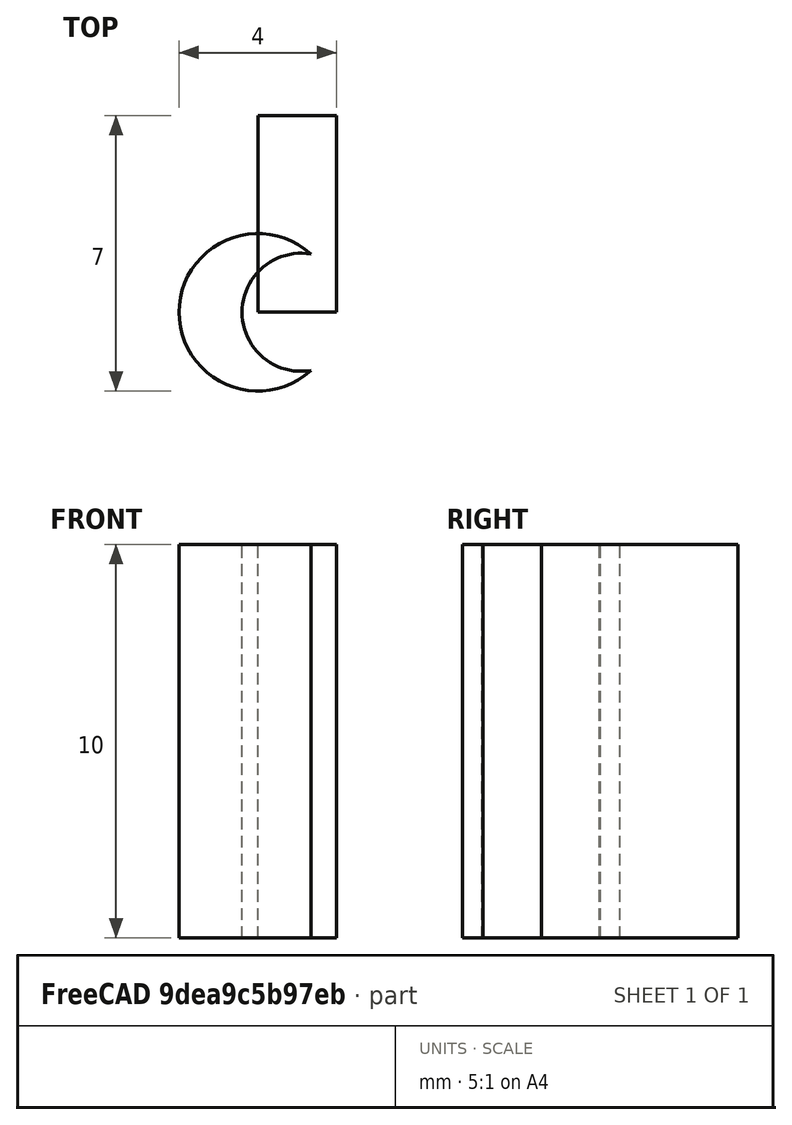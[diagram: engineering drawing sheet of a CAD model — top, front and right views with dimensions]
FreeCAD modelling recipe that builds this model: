
FCSTD DOCUMENT  (FreeCAD 0.17R11508 (Git))
Label: cylinderAFo
License: All rights reserved
LicenseURL: http://en.wikipedia.org/wiki/All_rights_reserved
objects: Fem::FemSolverObjectPython×2, App::MaterialObjectPython×2, Fem::ConstraintDisplacement×2, Fem::ConstraintFixed×2, Fem::FemMeshObjectPython×2, Fem::FemResultObjectPython×2, Fem::FemAnalysisPython×2, Part::Feature×1, Part::Box×1
note: 2 computed .brp shape members not serialized (recipe doc carries the construction recipe); baked Part::Feature solids carry a one-line shape summary decoded from their .brp

FEATURE [Fem::FemSolverObjectPython] CalculiX  # FEM object (typed FeaturePython)
  AnalysisType = 0
  EigenmodeHighLimit = 1000000
  EigenmodeLowLimit = 0
  EigenmodesCount = 10
  GeometricalNonlinearity = 0
  IterationsControlParameterCutb = 0.25,0.5,0.75,0.85,,,1.5,
  IterationsControlParameterIter = 4,8,9,200,10,400,,200,,
  IterationsControlParameterTimeUse = false
  IterationsThermoMechMaximum = 2000
  IterationsUserDefinedIncrementations = false
  IterationsUserDefinedTimeStepLength = false
  MaterialNonlinearity = 0
  MatrixSolverType = 0
  SolverType = FemSolverCalculix
  SplitInputWriter = false
  ThermoMechSteadyState = true
  TimeEnd = 1
  TimeInitialStep = 0.01
FEATURE [App::MaterialObjectPython] SolidMaterial  # material (typed FeaturePython)
  Category = 0
  Material = Density=1300.0 kg/m^3,+11 more (map truncated)
FEATURE [Part::Feature] Cut001
  shape: bbox 3.345 x 4 x 10 mm, 4 faces (baked)
FEATURE [Fem::ConstraintDisplacement] FemConstraintDisplacement
  NormalDirection = (0,0,1)
  Normals = (1) [(0,0,1)]
  Points = (1) [(-2,0,10)]
  References = -> [Cut001]
  rotxFix = false
  rotxFree = false
  rotyFix = false
  rotyFree = true
  rotzFix = true
  rotzFree = false
  xDisplacement = -0.0541705
  xFix = false
  xFree = false
  xRotation = 10
  yDisplacement = 0.0230125
  yFix = false
  yFree = false
  yRotation = 0
  zDisplacement = 0.00226832
  zFix = false
  zFree = false
  zRotation = 50
FEATURE [Fem::ConstraintFixed] FemConstraintFixed
  NormalDirection = (0,0,-1)
  Normals = (1) [(0,0,-1)]
  Points = (1) [(-2,0,0)]
  References = -> [Cut001]
FEATURE [Fem::FemMeshObjectPython] FEMMeshGMSH  # FEM object (typed FeaturePython)
  Algorithm2D = 0
  Algorithm3D = 0
  CharacteristicLengthMax = 0
  CharacteristicLengthMin = 0
  CoherenceMesh = true
  ElementDimension = 0
  ElementOrder = 1
  GeometryTolerance = 1e-06
  HighOrderOptimize = false
  OptimizeNetgen = false
  OptimizeStd = true
  Part = -> Cut001
  RecombineAll = false
FEATURE [Fem::FemResultObjectPython] CalculiX_static_results  # FEM object (typed FeaturePython)
  DisplacementLengths = [0.0588996,0.0588996,0,0,0.0588996,0.0588996,0.0588996,0.0588996,0.0588996,0.0588996,0.0588996,0.013727,0.0273456,0.0407869,0.0515742,0.00728433,0.0203832,0.0341927,0.0467081,0.0551273,0,0,0,0,0,0,0,0.0101896,0.0242184,0.0402139,0.0533005,+271 more]
  DisplacementVectors = (302) [(-0.0541705,0.0230125,0.00226832),(-0.0541705,0.0230125,0.00226832),(0,0,0),(0,0,0),(-0.0541705,0.0230125,0.00226832),+297 more]
  Eigenmode = 0
  EigenmodeFrequency = 0
  MaxShear = [5.5501,9.78783,10.6198,6.36073,3.63674,5.02008,1.77972,0.767103,5.05763,2.59359,5.59522,7.77964,3.28659,2.6727,7.10986,9.93378,5.64332,0.767785,4.88157,9.01165,2.95717,4.62495,2.19645,1.20809,4.42554,2.1266,5.85524,5.90892,2.41082,1.59936,+272 more]
  Mesh = -> FEMMeshGMSH
  NodeNumbers = [1,2,3,4,5,6,7,8,9,10,11,12,13,14,15,16,17,18,19,20,21,22,23,24,25,26,27,28,29,30,31,32,33,34,35,36,37,38,39,40,41,42,43,44,45,46,47,48,49,50,51,52,53,54,55,56,57,58,59,60,61,62,63,64,65,66,67,68,69,+233 more]
  PrincipalMax = [-3.16561,-4.33294,25.5958,16.2608,11.3628,17.2628,-0.330382,-0.302449,20.1892,9.8337,-3.99133,15.0806,6.56805,0.291143,0.37496,18.3907,11.0801,1.54534,0.552377,0.824055,-3.63394,-6.69301,5.5292,3.45117,-8.94039,-3.3151,17.4186,11.6049,+274 more]
  PrincipalMed = [-5.2038,-9.5514,9.6445,6.25228,4.92049,7.73802,-1.41141,-0.916493,10.8538,5.33106,-6.73552,0.682284,0.0931949,0.0262324,-0.0293278,0.690424,0.0876384,0.32165,0.167359,-1.33784,-4.2703,-7.25013,2.14533,1.86964,-9.63158,-4.03354,8.35848,+275 more]
  PrincipalMin = [-14.2658,-23.9086,4.35625,3.53934,4.08931,7.22268,-3.88982,-1.83666,10.0739,4.64653,-15.1818,-0.478681,-0.00512452,-5.05426,-13.8448,-1.47687,-0.206507,0.00976902,-9.21075,-17.1993,-9.54829,-15.9429,1.13631,1.035,-17.7915,-7.56831,5.70807,+275 more]
  ResultType = FemResultMechanical
  Stats = [-0.0541705,-0.0273203,0,-0.000334248,0.0115734,0.023171,-0.00876269,0.00251576,0.0171067,0,0.0302706,0.0588996,0.879918,5.38831,19.1511,-8.94039,3.31382,25.5958,-9.63158,0.0830932,10.8538,-23.9086,-2.44273,10.0739,0.503887,2.87828,10.6198,+3 more]
  StrainVectors = (302) [(0.000301202,0.00103919,-0.00308157),(0.000373942,0.00173259,-0.00501368),(-0.000367074,-0.00210085,0.00551382),(-0.000268967,-0.00119888,0.00347188),+298 more]
  StressValues = [10.2345,17.558,19.1511,11.6053,6.89557,9.79266,3.16075,1.33745,9.74874,4.88105,10.1019,15.0125,6.52457,5.21799,14.0219,18.8774,11.1425,1.40582,9.57643,17.0455,5.62324,8.98431,3.98536,2.12553,8.52652,3.94338,10.6359,11.627,4.7571,3.11266,+272 more]
  StressVectors = (302) [(-5.18552,-3.21031,-14.2394),(-9.00316,-5.36678,-23.423),(9.499,4.8586,25.239),(6.17635,3.68747,16.1886),(4.72561,4.47797,11.169),+297 more]
  Time = 0
FEATURE [Fem::FemAnalysisPython] Analysis001  # FEM object (typed FeaturePython)
  Member = -> [SolidMaterial,CalculiX,FemConstraintFixed,FemConstraintDisplacement,FEMMeshGMSH,CalculiX_static_results]
FEATURE [Part::Box] Box  label="Cube"
  AttacherType = Attacher::AttachEngine3D
  Height = 10
  Length = 2
  Width = 5
FEATURE [Fem::FemSolverObjectPython] CalculiX001  # FEM object (typed FeaturePython)
  AnalysisType = 0
  EigenmodeHighLimit = 1000000
  EigenmodeLowLimit = 0
  EigenmodesCount = 10
  GeometricalNonlinearity = 0
  IterationsControlParameterCutb = 0.25,0.5,0.75,0.85,,,1.5,
  IterationsControlParameterIter = 4,8,9,200,10,400,,200,,
  IterationsControlParameterTimeUse = false
  IterationsThermoMechMaximum = 2000
  IterationsUserDefinedIncrementations = false
  IterationsUserDefinedTimeStepLength = false
  MaterialNonlinearity = 0
  MatrixSolverType = 0
  SolverType = FemSolverCalculix
  SplitInputWriter = false
  ThermoMechSteadyState = true
  TimeEnd = 1
  TimeInitialStep = 0.01
FEATURE [Fem::FemMeshObjectPython] FEMMeshGMSH001  # FEM object (typed FeaturePython)
  Algorithm2D = 0
  Algorithm3D = 0
  CharacteristicLengthMax = 0
  CharacteristicLengthMin = 0
  CoherenceMesh = true
  ElementDimension = 0
  ElementOrder = 1
  GeometryTolerance = 1e-06
  HighOrderOptimize = false
  OptimizeNetgen = false
  OptimizeStd = true
  Part = -> Box
  RecombineAll = false
FEATURE [Fem::ConstraintFixed] FemConstraintFixed001
  NormalDirection = (0,0,-1)
  Normals = (9) [(0,0,-1),(0,0,-1),(0,0,-1),(0,0,-1),(0,0,-1),(0,0,-1),(0,0,-1),(0,0,-1),(0,0,-1)]
  Points = (9) [(0,0,0),(1,0,0),(2,0,0),(0,2.5,0),(1,2.5,0),(2,2.5,0),(0,5,0),(1,5,0),(2,5,0)]
  References = -> [Box]
FEATURE [Fem::ConstraintDisplacement] FemConstraintDisplacement001
  NormalDirection = (0,0,1)
  Normals = (9) [(0,0,1),(0,0,1),(0,0,1),(0,0,1),(0,0,1),(0,0,1),(0,0,1),(0,0,1),(0,0,1)]
  Points = (9) [(0,0,10),(1,0,10),(2,0,10),(0,2.5,10),(1,2.5,10),(2,2.5,10),(0,5,10),(1,5,10),(2,5,10)]
  References = -> [Box]
  rotxFix = false
  rotxFree = true
  rotyFix = false
  rotyFree = true
  rotzFix = false
  rotzFree = true
  xDisplacement = -0.0772818
  xFix = false
  xFree = false
  xRotation = 0
  yDisplacement = -0.0305455
  yFix = false
  yFree = true
  yRotation = 0
  zDisplacement = -0.0367532
  zFix = false
  zFree = false
  zRotation = 0
FEATURE [App::MaterialObjectPython] SolidMaterial001  # material (typed FeaturePython)
  Category = 0
  Material = Density=1300.0 kg/m^3,+11 more (map truncated)
FEATURE [Fem::FemResultObjectPython] CalculiX_static_results001  # FEM object (typed FeaturePython)
  DisplacementLengths = [0.0855981,0,0.0855979,0,0.085794,0,0.0857923,0,0.0100211,0.0191373,0.0302149,0.042767,0.0556271,0.0677889,0.0779834,0.0847519,0.00593435,0.0143465,0.0244409,0.0363452,0.0492111,0.0618743,0.0732136,0.0819048,0.0861081,0.0855867,0.0855774,+1140 more]
  DisplacementVectors = (1167) [(-0.0772818,-0.00194122,-0.0367532),(0,0,0),(-0.0772818,0.00192855,-0.0367532),(0,0,0),(-0.0772818,-0.00610989,-0.0367532),(0,0,0),+1161 more]
  Eigenmode = 0
  EigenmodeFrequency = 0
  MaxShear = [3.50868,14.5207,3.49244,14.5548,13.5331,3.42439,13.5651,3.53475,11.8169,10.8661,9.31708,7.82255,6.00402,4.24455,2.51005,0.587048,13.686,11.3918,10.1302,8.58794,6.90412,5.16287,3.39081,1.56804,1.37909,1.36531,1.30545,1.61262,1.21112,2.11705,+1137 more]
  Mesh = -> FEMMeshGMSH001
  NodeNumbers = [1,2,3,4,5,6,7,8,9,10,11,12,13,14,15,16,17,18,19,20,21,22,23,24,25,26,27,28,29,30,31,32,33,34,35,36,37,38,39,40,41,42,43,44,45,46,47,48,49,50,51,52,53,54,55,56,57,58,59,60,61,62,63,64,65,66,67,68,69,+1098 more]
  PrincipalMax = [3.36479,-13.0002,3.40638,-12.9645,-1.14695,1.2455,-1.18486,1.38422,1.24917,0.138364,0.0630202,0.0988598,0.0117695,0.000412563,0.145215,0.362612,-0.366718,0.272135,0.1634,0.102216,0.0730308,0.0527588,0.0900072,0.0860648,1.13967,3.62537,+1141 more]
  PrincipalMed = [-1.43031,-14.9856,-1.42898,-15.0093,-7.29047,-2.00101,-7.39752,-2.01041,1.00061,0.0680773,-0.0915688,-0.001559,0.00178862,-0.0332956,-0.0356703,0.116552,-0.798133,-0.0901178,0.0495771,-0.020966,-0.00278669,-0.0362519,-0.103638,-0.0425955,+1143 more]
  PrincipalMin = [-3.65256,-42.0416,-3.57849,-42.0742,-28.2132,-5.60327,-28.3151,-5.68528,-22.3845,-21.5938,-18.5711,-15.5462,-11.9963,-8.48868,-4.87488,-0.811484,-27.7386,-22.5115,-20.097,-17.0737,-13.7352,-10.273,-6.69161,-3.05001,-1.61852,0.894742,+1141 more]
  ResultType = FemResultMechanical
  Stats = [-0.0778994,-0.0386673,0.000462407,-0.00610989,-8.63561e-06,0.00608627,-0.036824,-0.0182783,0.000478762,0,0.0432837,0.0861081,0.582172,13.4809,28.3789,-17.198,-0.088132,6.31633,-20.9176,-1.29658,3.9954,-42.0742,-14.0291,3.69996,0.320897,+5 more]
  StrainVectors = (1167) [(-0.000271674,0.000336585,-0.000197071),(0.000961069,0.00101202,-0.00735981),(-0.00028464,0.00036483,-0.000203352),+1164 more]
  StressValues = [6.21187,28.1014,6.19635,28.1431,24.5773,5.93388,24.619,6.12397,23.5104,21.6971,18.5574,15.5951,12.0031,8.47229,4.93214,1.07245,27.1588,22.6047,20.2038,17.1146,13.7705,10.2815,6.6869,3.07377,2.39922,2.49537,2.53328,2.85505,2.27764,3.75839,+1137 more]
  StressVectors = (1167) [(-1.18192,0.446072,-0.982241),(-15.9644,-15.828,-38.235),(-1.18565,0.552636,-0.968086),(-16.0047,-15.8828,-38.1605),(-7.13836,-1.52343,-27.9888),+1162 more]
  Time = 0
FEATURE [Fem::FemAnalysisPython] Analysis  # FEM object (typed FeaturePython)
  Member = -> [CalculiX001,FEMMeshGMSH001,FemConstraintFixed001,FemConstraintDisplacement001,SolidMaterial001,CalculiX_static_results001]
